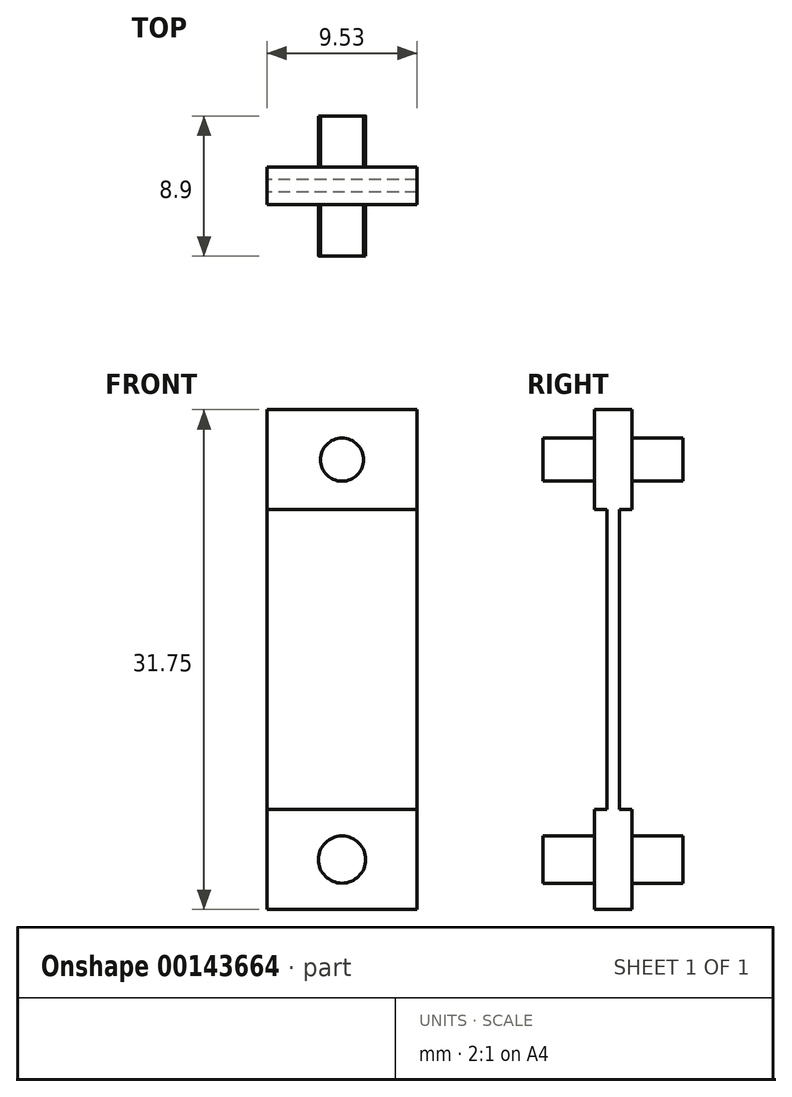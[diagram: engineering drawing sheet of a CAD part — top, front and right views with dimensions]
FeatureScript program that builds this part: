
annotation { "Feature Type Name" : "Feature", "Feature Type Description" : "" }
export const myFeature = defineFeature(function(context is Context, id is Id, definition is map)
    precondition{}
    {
        {
            var Q0;
            Q0=qCreatedBy(makeId("Front.planeOp"),FACE);
            var sketch = newSketch(context, id + "F0", { "sketchPlane" : qUnion([Q0])});
            skLineSegment(sketch, "E0.bottom", {"start": v(-30, 47.14) * mm, "end": v(-20.47, 47.14) * mm});
            skLineSegment(sketch, "E0.top", {"start": v(-30, 15.39) * mm, "end": v(-20.47, 15.39) * mm});
            skLineSegment(sketch, "E0.left", {"start": v(-30, 47.14) * mm, "end": v(-30, 15.39) * mm});
            skLineSegment(sketch, "E0.right", {"start": v(-20.47, 47.14) * mm, "end": v(-20.47, 15.39) * mm});
            skLineSegment(sketch, "E1", {"start": v(-20.47, 40.79) * mm, "end": v(-30, 40.79) * mm});
            skLineSegment(sketch, "E2", {"start": v(-20.47, 21.74) * mm, "end": v(-30, 21.74) * mm});
            skCircle(sketch, "E3", {"center": v(-25.24, 43.96) * mm, "radius": 1.37 * mm});
            skCircle(sketch, "E4", {"center": v(-25.24, 18.56) * mm, "radius": 1.5 * mm});
            skSolve(sketch);
        }
        {
            var Q0;
            {var subQ0=sQuery(id+"F0.wireOp",EDGE,"E1");Q0=makeQuery(id+"F0.imprint","IMPRINT",FACE,{"disambiguationData":[TD([[makeQuery(id+"F0.imprint","IMPRINT",EDGE,{"derivedFrom":subQ0}),1.0]])]});}
            extrude(context, id + "F1", {"entities" : qUnion([Q0]), "endBound" : BoundingType.SYMMETRIC, "depth" : 0.8 * mm});
        }
        {
            var Q0;
            {var subQ2=sQuery(id+"F0.wireOp",EDGE,"E0.top");Q0=makeQuery(id+"F0.imprint","IMPRINT",FACE,{"disambiguationData":[TD([[makeQuery(id+"F0.imprint","IMPRINT",EDGE,{"derivedFrom":subQ2}),1.0]])]});}
            var Q1;
            {var subQ2=sQuery(id+"F0.wireOp",EDGE,"E0.bottom");Q1=makeQuery(id+"F0.imprint","IMPRINT",FACE,{"disambiguationData":[TD([[makeQuery(id+"F0.imprint","IMPRINT",EDGE,{"derivedFrom":subQ2}),-1.0]])]});}
            extrude(context, id + "F2", {"entities" : qUnion([Q0, Q1]), "operationType" : NewBodyOperationType.ADD, "endBound" : BoundingType.SYMMETRIC, "depth" : 2.38 * mm});
        }
        {
            var Q0;
            Q0=makeQuery(id+"F0.imprint","IMPRINT",FACE,{"disambiguationData":[TD([[makeQuery(id+"F0.imprint","IMPRINT",EDGE,{"derivedFrom":sQuery(id+"F0.wireOp",EDGE,"E3")}),1.0]])]});
            var Q1;
            Q1=makeQuery(id+"F0.imprint","IMPRINT",FACE,{"disambiguationData":[TD([[makeQuery(id+"F0.imprint","IMPRINT",EDGE,{"derivedFrom":sQuery(id+"F0.wireOp",EDGE,"E4")}),1.0]])]});
            extrude(context, id + "F3", {"entities" : qUnion([Q0, Q1]), "operationType" : NewBodyOperationType.ADD, "endBound" : BoundingType.SYMMETRIC, "depth" : 8.9 * mm});
        }
    });
